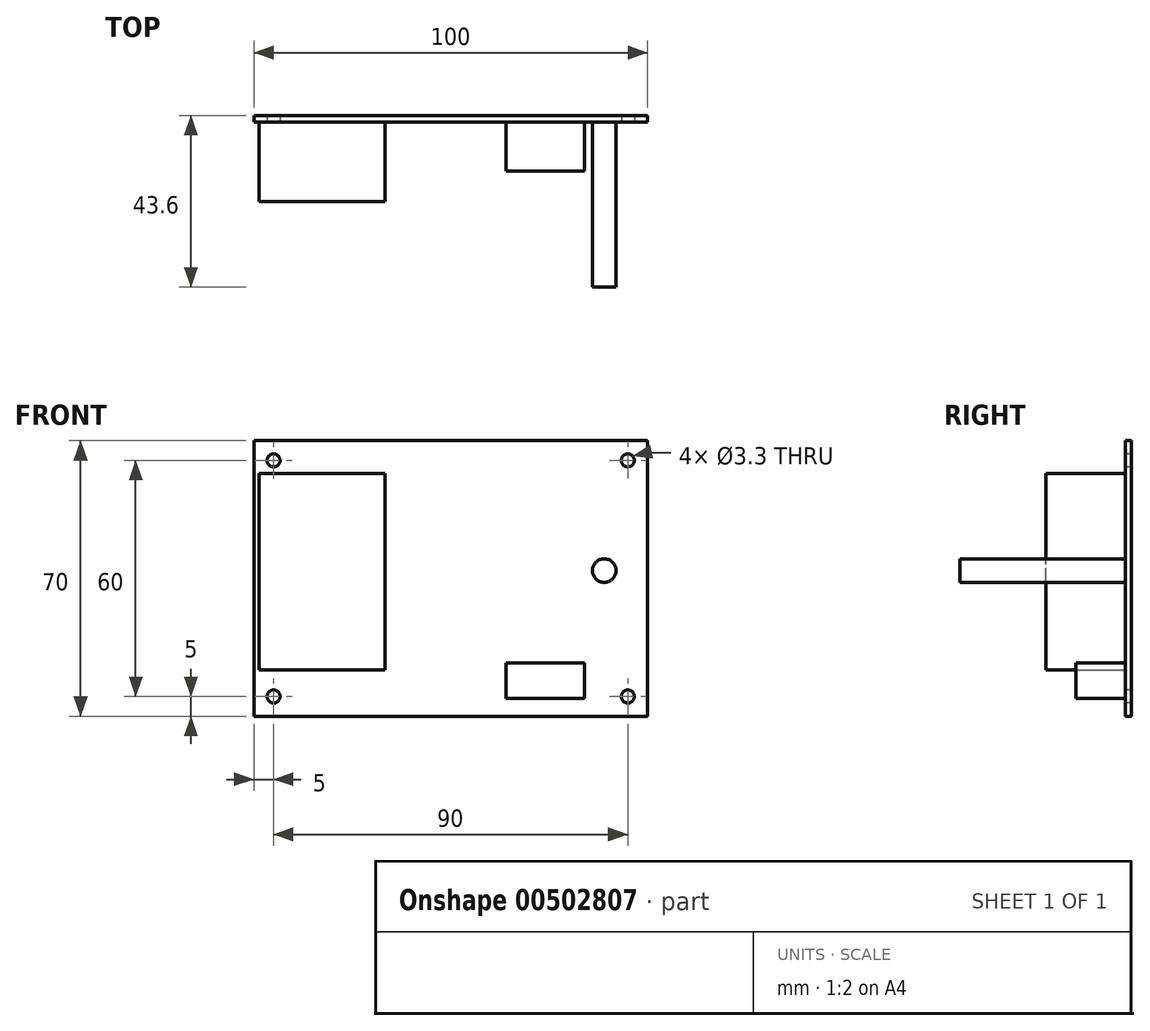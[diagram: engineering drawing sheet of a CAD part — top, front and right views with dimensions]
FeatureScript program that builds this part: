
annotation { "Feature Type Name" : "Feature", "Feature Type Description" : "" }
export const myFeature = defineFeature(function(context is Context, id is Id, definition is map)
    precondition{}
    {
        {
            var Q0;
            Q0=qCreatedBy(makeId("Front.planeOp"),FACE);
            var sketch = newSketch(context, id + "F0", { "sketchPlane" : qUnion([Q0])});
            skLineSegment(sketch, "E0.bottom", {"start": v(-50, 35) * mm, "end": v(50, 35) * mm});
            skLineSegment(sketch, "E0.top", {"start": v(-50, -35) * mm, "end": v(50, -35) * mm});
            skLineSegment(sketch, "E0.left", {"start": v(-50, 35) * mm, "end": v(-50, -35) * mm});
            skLineSegment(sketch, "E0.right", {"start": v(50, 35) * mm, "end": v(50, -35) * mm});
            skPoint(sketch, "E0.middle", {"position": v(0, 0) * mm});
            skPoint(sketch, "E1", {"position": v(-45, 30) * mm});
            skPoint(sketch, "E2", {"position": v(45, 30) * mm});
            skPoint(sketch, "E3", {"position": v(-45, -30) * mm});
            skPoint(sketch, "E4", {"position": v(45, -30) * mm});
            skLineSegment(sketch, "E5", {"start": v(0, 48.14) * mm, "end": v(0, -44.05) * mm, "construction": true});
            skLineSegment(sketch, "E6", {"start": v(-67.66, 0) * mm, "end": v(55.1, 0) * mm, "construction": true});
            skPoint(sketch, "E7", {"position": v(0, 30) * mm});
            skPoint(sketch, "E8", {"position": v(-45, 0) * mm});
            skCircle(sketch, "E9", {"center": v(39, 2) * mm, "radius": 3 * mm});
            skLineSegment(sketch, "E10.bottom", {"start": v(34, -30.5) * mm, "end": v(14, -30.5) * mm});
            skLineSegment(sketch, "E10.top", {"start": v(34, -21.5) * mm, "end": v(14, -21.5) * mm});
            skLineSegment(sketch, "E10.left", {"start": v(34, -30.5) * mm, "end": v(34, -21.5) * mm});
            skLineSegment(sketch, "E10.right", {"start": v(14, -30.5) * mm, "end": v(14, -21.5) * mm});
            skPoint(sketch, "E10.middle", {"position": v(24, -26) * mm});
            skLineSegment(sketch, "E11.bottom", {"start": v(-16.7, -23.3) * mm, "end": v(-48.7, -23.3) * mm});
            skLineSegment(sketch, "E11.top", {"start": v(-16.7, 26.7) * mm, "end": v(-48.7, 26.7) * mm});
            skLineSegment(sketch, "E11.left", {"start": v(-16.7, -23.3) * mm, "end": v(-16.7, 26.7) * mm});
            skLineSegment(sketch, "E11.right", {"start": v(-48.7, -23.3) * mm, "end": v(-48.7, 26.7) * mm});
            skPoint(sketch, "E11.middle", {"position": v(-32.7, 1.7) * mm});
            skCircle(sketch, "E12", {"center": v(-45, 30) * mm, "radius": 1.65 * mm});
            skCircle(sketch, "E13", {"center": v(45, 30) * mm, "radius": 1.65 * mm});
            skCircle(sketch, "E14", {"center": v(45, -30) * mm, "radius": 1.65 * mm});
            skCircle(sketch, "E15", {"center": v(-45, -30) * mm, "radius": 1.65 * mm});
            skSolve(sketch);
        }
        {
            var Q0;
            Q0=makeQuery(id+"F0.imprint","IMPRINT",FACE,{"disambiguationData":[TD([[makeQuery(id+"F0.imprint","IMPRINT",EDGE,{"derivedFrom":sQuery(id+"F0.wireOp",EDGE,"E0.bottom")}),-1.0]])]});
            var Q1;
            Q1=makeQuery(id+"F0.imprint","IMPRINT",FACE,{"disambiguationData":[TD([[makeQuery(id+"F0.imprint","IMPRINT",EDGE,{"derivedFrom":sQuery(id+"F0.wireOp",EDGE,"E11.bottom")}),-1.0]])]});
            var Q2;
            Q2=makeQuery(id+"F0.imprint","IMPRINT",FACE,{"disambiguationData":[TD([[makeQuery(id+"F0.imprint","IMPRINT",EDGE,{"derivedFrom":sQuery(id+"F0.wireOp",EDGE,"E10.bottom")}),-1.0]])]});
            var Q3;
            Q3=makeQuery(id+"F0.imprint","IMPRINT",FACE,{"disambiguationData":[TD([[makeQuery(id+"F0.imprint","IMPRINT",EDGE,{"derivedFrom":sQuery(id+"F0.wireOp",EDGE,"E9")}),1.0]])]});
            extrude(context, id + "F1", {"entities" : qUnion([Q0, Q1, Q2, Q3]), "oppositeDirection" : true, "depth" : 1.6 * mm});
        }
        {
            var Q0;
            Q0=makeQuery(id+"F0.imprint","IMPRINT",FACE,{"disambiguationData":[TD([[makeQuery(id+"F0.imprint","IMPRINT",EDGE,{"derivedFrom":sQuery(id+"F0.wireOp",EDGE,"E11.bottom")}),-1.0]])]});
            extrude(context, id + "F2", {"entities" : qUnion([Q0]), "operationType" : NewBodyOperationType.ADD, "depth" : 20.2 * mm});
        }
        {
            var Q0;
            Q0=makeQuery(id+"F0.imprint","IMPRINT",FACE,{"disambiguationData":[TD([[makeQuery(id+"F0.imprint","IMPRINT",EDGE,{"derivedFrom":sQuery(id+"F0.wireOp",EDGE,"E10.bottom")}),-1.0]])]});
            extrude(context, id + "F3", {"entities" : qUnion([Q0]), "operationType" : NewBodyOperationType.ADD, "depth" : 12.5 * mm});
        }
        {
            var Q0;
            Q0=makeQuery(id+"F0.imprint","IMPRINT",FACE,{"disambiguationData":[TD([[makeQuery(id+"F0.imprint","IMPRINT",EDGE,{"derivedFrom":sQuery(id+"F0.wireOp",EDGE,"E9")}),1.0]])]});
            extrude(context, id + "F4", {"entities" : qUnion([Q0]), "operationType" : NewBodyOperationType.ADD, "depth" : 42 * mm});
        }
    });
